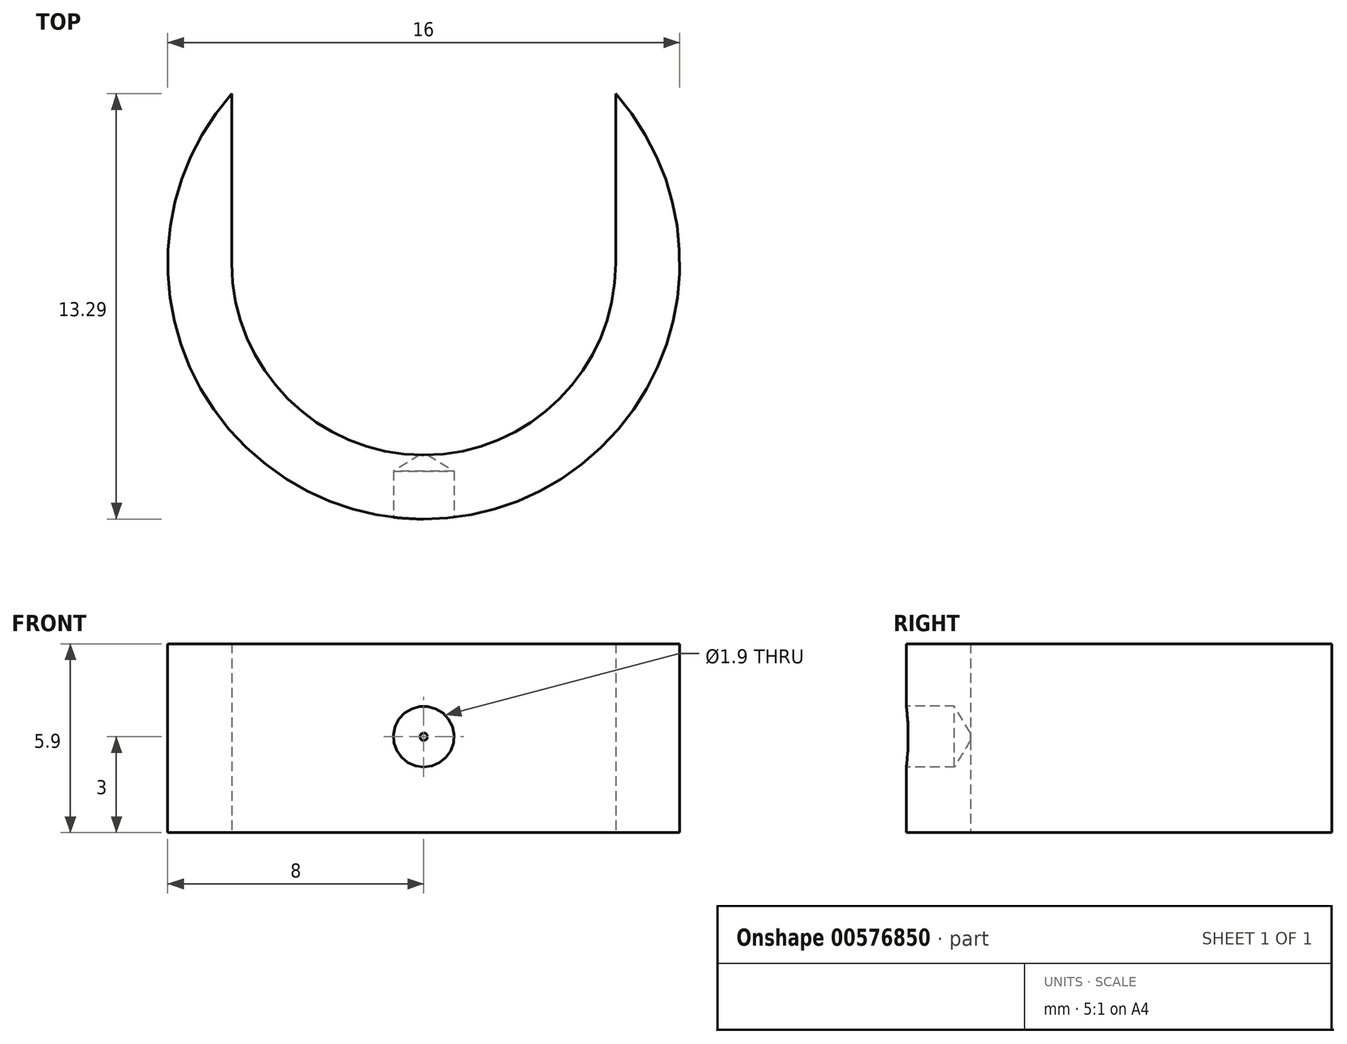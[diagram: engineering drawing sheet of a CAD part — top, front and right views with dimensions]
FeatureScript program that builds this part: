
annotation { "Feature Type Name" : "Feature", "Feature Type Description" : "" }
export const myFeature = defineFeature(function(context is Context, id is Id, definition is map)
    precondition{}
    {
        {
            var Q0;
            Q0=qCreatedBy(makeId("Top.planeOp"),FACE);
            var sketch = newSketch(context, id + "F0", { "sketchPlane" : qUnion([Q0])});
            skLineSegment(sketch, "E0", {"start": v(0, 0) * mm, "end": v(6, 0) * mm, "construction": true});
            skLineSegment(sketch, "E1", {"start": v(0, 0) * mm, "end": v(-6, 0) * mm, "construction": true});
            skLineSegment(sketch, "E2", {"start": v(-6, 0) * mm, "end": v(-6, 5.3) * mm});
            skLineSegment(sketch, "E3", {"start": v(6, 0) * mm, "end": v(6, 5.3) * mm});
            skArc(sketch, "E4", {"start": v(-6, 0) * mm, "mid": v(0, -6) * mm, "end": v(6, 0) * mm});
            skArc(sketch, "E5", {"start": v(-6, 5.3) * mm, "mid": v(0, -8) * mm, "end": v(6, 5.3) * mm});
            skSolve(sketch);
        }
        {
            var Q0;
            Q0 = qSketchRegion(id + "F0", true);
            extrude(context, id + "F1", {"entities" : qUnion([Q0]), "depth" : 5.9 * mm, "offsetDistance" : 25 * mm});
        }
        {
            var Q0;
            Q0=qCreatedBy(makeId("Front.planeOp"),FACE);
            cPlane(context, id + "F2", {"entities" : qUnion([Q0]), "cplaneType" : CPlaneType.OFFSET, "offset" : 8 * mm, "width" : 150 * mm, "height" : 150 * mm});
        }
        {
            var Q0;
            Q0=qCreatedBy(id+"F2.planeOp",FACE);
            var sketch = newSketch(context, id + "F3", { "sketchPlane" : qUnion([Q0])});
            skLineSegment(sketch, "E6", {"start": v(0, 0) * mm, "end": v(0, 3) * mm, "construction": true});
            skSolve(sketch);
        }
        {
            var Q0;
            Q0=sQuery(id+"F3.wireOp",VERTEX,"E6.end");
            var Q1;
            Q1=makeQuery(id+"F1.opExtrude","SWEPT_BODY",BODY,{"disambiguationData":[OSD([sQuery(id+"F0.wireOp",EDGE,"E2"),sQuery(id+"F0.wireOp",EDGE,"E3"),sQuery(id+"F0.wireOp",EDGE,"E4"),sQuery(id+"F0.wireOp",EDGE,"E5")])]});
            hole(context, id + "F4", {"style" : HoleStyle.C_SINK, "endStyle" : HoleEndStyle.BLIND, "holeDiameter" : 1.9 * mm, "cSinkDiameter" : 1.9 * mm, "cSinkAngle" : 90 * degree, "holeDepth" : 1.5 * mm, "isTappedThrough" : true, "tappedDepth" : 12 * mm, "tapClearance" : 3, "startFromSketch" : true, "locations" : qUnion([Q0]), "scope" : qUnion([Q1])});
        }
    });
